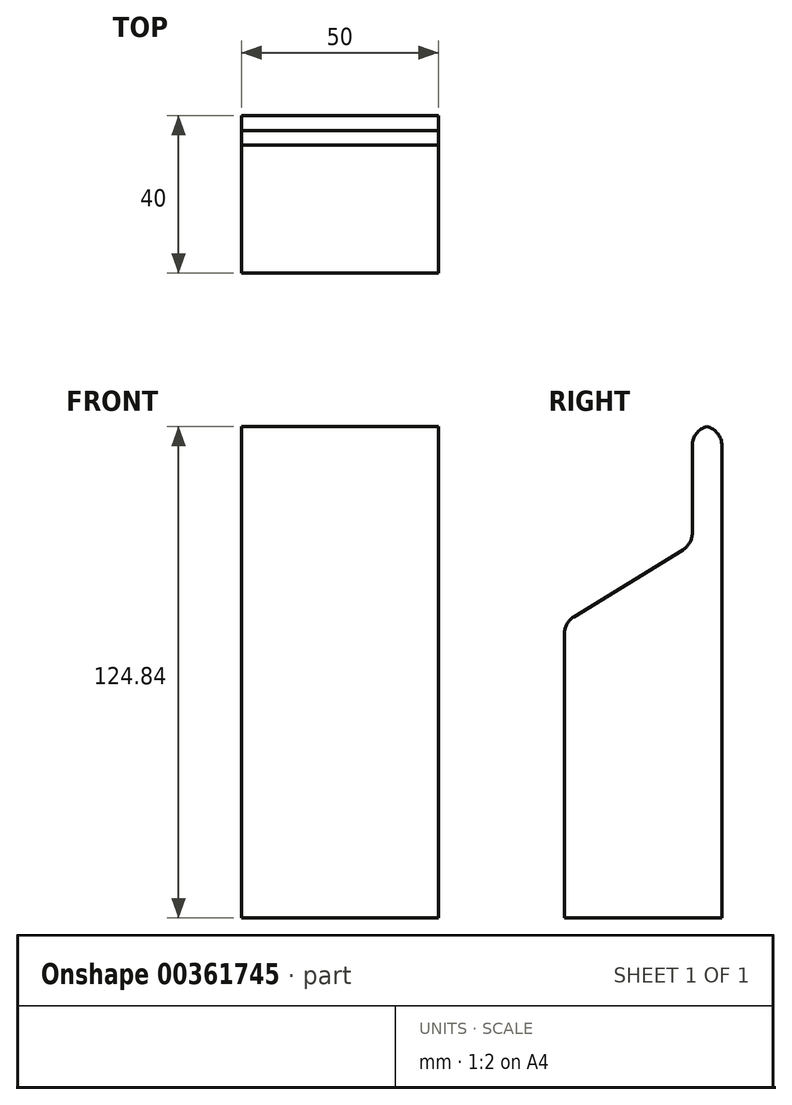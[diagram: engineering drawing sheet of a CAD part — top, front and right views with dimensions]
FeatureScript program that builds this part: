
annotation { "Feature Type Name" : "Feature", "Feature Type Description" : "" }
export const myFeature = defineFeature(function(context is Context, id is Id, definition is map)
    precondition{}
    {
        {
            var Q0;
            Q0=qCreatedBy(makeId("Right.planeOp"),FACE);
            var sketch = newSketch(context, id + "F0", { "sketchPlane" : qUnion([Q0])});
            skLineSegment(sketch, "E0", {"start": v(-32.5, -50.58) * mm, "end": v(-32.5, 24.42) * mm});
            skLineSegment(sketch, "E1", {"start": v(-32.5, 24.42) * mm, "end": v(0, 44.42) * mm});
            skLineSegment(sketch, "E2", {"start": v(0, 44.42) * mm, "end": v(0, 74.42) * mm});
            skLineSegment(sketch, "E3", {"start": v(0, 74.42) * mm, "end": v(7.5, 74.42) * mm});
            skLineSegment(sketch, "E4", {"start": v(7.5, 74.42) * mm, "end": v(7.5, -50.58) * mm});
            skLineSegment(sketch, "E5", {"start": v(7.5, -50.58) * mm, "end": v(-32.5, -50.58) * mm});
            skSolve(sketch);
        }
        {
            var Q0;
            Q0=makeQuery(id+"F0.imprint","IMPRINT",FACE,{"disambiguationData":[TD([[makeQuery(id+"F0.imprint","IMPRINT",EDGE,{"derivedFrom":sQuery(id+"F0.wireOp",EDGE,"E0")}),-1.0]])]});
            extrude(context, id + "F1", {"entities" : qUnion([Q0]), "depth" : 50 * mm});
        }
        {
            var Q0;
            Q0=makeQuery(id+"F1.opExtrude","SWEPT_EDGE",EDGE,{"disambiguationData":[OSD([sQuery(id+"F0.wireOp",EDGE,"E2"),sQuery(id+"F0.wireOp",EDGE,"E3")])]});
            var Q1;
            Q1=makeQuery(id+"F1.opExtrude","SWEPT_EDGE",EDGE,{"disambiguationData":[OSD([sQuery(id+"F0.wireOp",EDGE,"E3"),sQuery(id+"F0.wireOp",EDGE,"E4")])]});
            var Q2;
            Q2=makeQuery(id+"F1.opExtrude","SWEPT_EDGE",EDGE,{"disambiguationData":[OSD([sQuery(id+"F0.wireOp",EDGE,"E1"),sQuery(id+"F0.wireOp",EDGE,"E2")])]});
            var Q3;
            Q3=makeQuery(id+"F1.opExtrude","SWEPT_EDGE",EDGE,{"disambiguationData":[OSD([sQuery(id+"F0.wireOp",EDGE,"E0"),sQuery(id+"F0.wireOp",EDGE,"E1")])]});
            fillet(context, id + "F2", {"entities" : qUnion([Q0, Q1, Q2, Q3]), "radius" : 5 * mm, "tangentPropagation" : true, "allowEdgeOverflow" : false});
        }
    });
